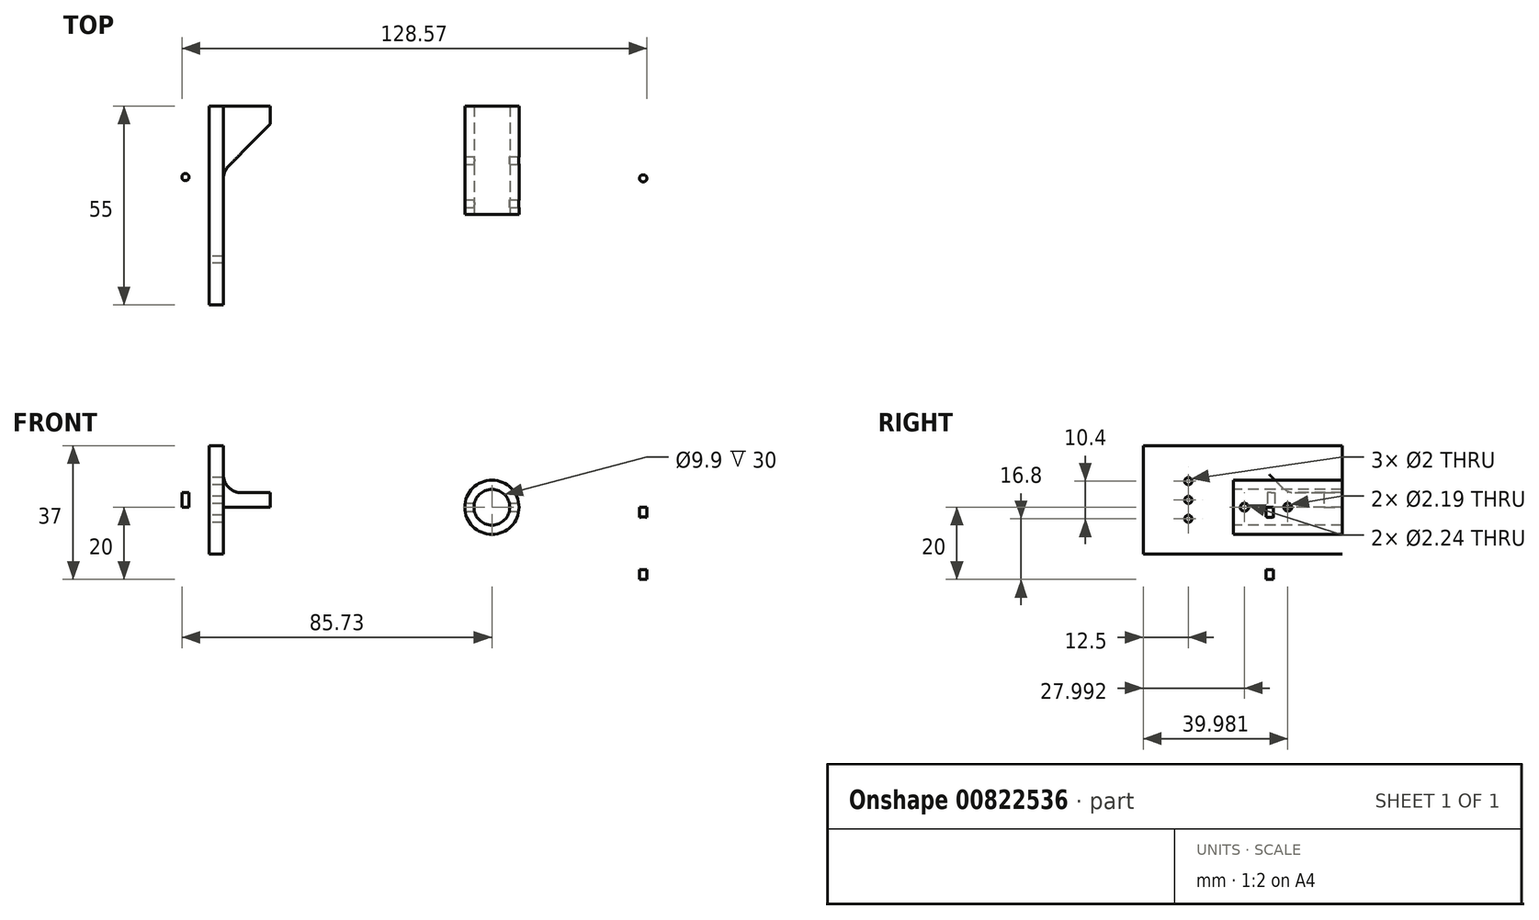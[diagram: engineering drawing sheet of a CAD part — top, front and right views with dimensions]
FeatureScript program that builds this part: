
annotation { "Feature Type Name" : "Feature", "Feature Type Description" : "" }
export const myFeature = defineFeature(function(context is Context, id is Id, definition is map)
    precondition{}
    {
        {
            var Q0;
            Q0=qCreatedBy(makeId("Front.planeOp"),FACE);
            var sketch = newSketch(context, id + "F0", { "sketchPlane" : qUnion([Q0])});
            skCircle(sketch, "E0", {"center": v(0, 0) * mm, "radius": 4.95 * mm});
            skCircle(sketch, "E1", {"center": v(0, 0) * mm, "radius": 7.5 * mm});
            skSolve(sketch);
        }
        {
            var Q0;
            Q0 = qSketchRegion(id + "F0", true);
            extrude(context, id + "F1", {"entities" : qUnion([Q0]), "oppositeDirection" : true, "depth" : 30 * mm, "offsetDistance" : 25 * mm});
        }
        {
            var Q0;
            Q0=qCreatedBy(makeId("Right.planeOp"),FACE);
            cPlane(context, id + "F2", {"entities" : qUnion([Q0]), "cplaneType" : CPlaneType.OFFSET, "offset" : 7.5 * mm, "width" : 150 * mm, "height" : 150 * mm});
        }
        {
            var Q0;
            Q0=qCreatedBy(id+"F2.planeOp",FACE);
            var sketch = newSketch(context, id + "F3", { "sketchPlane" : qUnion([Q0])});
            skLineSegment(sketch, "E2", {"start": v(0, 0) * mm, "end": v(29.96, 0) * mm});
            skLineSegment(sketch, "E3", {"start": v(14.98, 0) * mm, "end": v(14.98, 7.5) * mm});
            skCircle(sketch, "E4", {"center": v(14.98, 0) * mm, "radius": 1.1 * mm});
            skLineSegment(sketch, "E5", {"start": v(0, 0) * mm, "end": v(3, 0) * mm});
            skCircle(sketch, "E6", {"center": v(3, 0) * mm, "radius": 1.12 * mm});
            skSolve(sketch);
        }
        {
            var Q0;
            Q0 = qSketchRegion(id + "F3", true);
            extrude(context, id + "F4", {"entities" : qUnion([Q0]), "operationType" : NewBodyOperationType.REMOVE, "oppositeDirection" : true, "depth" : 25 * mm, "offsetDistance" : 25 * mm});
        }
        {
            var Q0;
            Q0=qCreatedBy(makeId("Front.planeOp"),FACE);
            var sketch = newSketch(context, id + "F5", { "sketchPlane" : qUnion([Q0])});
            skLineSegment(sketch, "E7.bottom", {"start": v(31.94, 0) * mm, "end": v(51.73, 0) * mm});
            skLineSegment(sketch, "E7.top", {"start": v(31.94, -20) * mm, "end": v(51.73, -20) * mm});
            skLineSegment(sketch, "E7.left", {"start": v(31.94, 0) * mm, "end": v(31.94, -20) * mm});
            skLineSegment(sketch, "E7.right", {"start": v(51.73, 0) * mm, "end": v(51.73, -20) * mm});
            skLineSegment(sketch, "E8", {"start": v(41.84, 0) * mm, "end": v(41.84, -20) * mm});
            skLineSegment(sketch, "E9", {"start": v(31.94, -10) * mm, "end": v(51.73, -10) * mm});
            skCircle(sketch, "E10", {"center": v(41.84, -10) * mm, "radius": 7.3 * mm});
            skSolve(sketch);
        }
        {
            var Q0;
            {var subQ1=sQuery(id+"F5.wireOp",EDGE,"E7.left");var subQ6=sQuery(id+"F5.wireOp",EDGE,"E7.bottom");var subQ9=makeQuery(id+"F5.imprint","INTERSECT",VERTEX,{"derivedFrom":[subQ6,subQ1]});Q0=makeQuery(id+"F5.imprint","IMPRINT",FACE,{"disambiguationData":[TD([[makeQuery(id+"F5.imprint","IMPRINT",EDGE,{"disambiguationData":[TD([[subQ9,-1.0]])],"derivedFrom":subQ6}),-1.0]])]});}
            var Q1;
            {var subQ1=sQuery(id+"F5.wireOp",EDGE,"E7.right");var subQ6=sQuery(id+"F5.wireOp",EDGE,"E7.bottom");var subQ9=makeQuery(id+"F5.imprint","INTERSECT",VERTEX,{"derivedFrom":[subQ6,subQ1]});Q1=makeQuery(id+"F5.imprint","IMPRINT",FACE,{"disambiguationData":[TD([[makeQuery(id+"F5.imprint","IMPRINT",EDGE,{"disambiguationData":[TD([[subQ9,1.0]])],"derivedFrom":subQ6}),-1.0]])]});}
            var Q2;
            {var subQ1=sQuery(id+"F5.wireOp",EDGE,"E7.right");var subQ6=sQuery(id+"F5.wireOp",EDGE,"E7.top");var subQ9=makeQuery(id+"F5.imprint","INTERSECT",VERTEX,{"derivedFrom":[subQ6,subQ1]});Q2=makeQuery(id+"F5.imprint","IMPRINT",FACE,{"disambiguationData":[TD([[makeQuery(id+"F5.imprint","IMPRINT",EDGE,{"disambiguationData":[TD([[subQ9,1.0]])],"derivedFrom":subQ6}),1.0]])]});}
            var Q3;
            {var subQ1=sQuery(id+"F5.wireOp",EDGE,"E7.top");var subQ5=sQuery(id+"F5.wireOp",EDGE,"E7.left");var subQ6=makeQuery(id+"F5.imprint","INTERSECT",VERTEX,{"derivedFrom":[subQ1,subQ5]});Q3=makeQuery(id+"F5.imprint","IMPRINT",FACE,{"disambiguationData":[TD([[makeQuery(id+"F5.imprint","IMPRINT",EDGE,{"disambiguationData":[TD([[subQ6,-1.0]])],"derivedFrom":subQ1}),1.0]])]});}
            extrude(context, id + "F6", {"entities" : qUnion([Q0, Q1, Q2, Q3]), "oppositeDirection" : true, "depth" : 20 * mm, "offsetDistance" : 25 * mm});
        }
        {
            var Q0;
            Q0=makeQuery(id+"F6.opExtrude","SWEPT_FACE",FACE,{"disambiguationData":[OSD([sQuery(id+"F5.wireOp",EDGE,"E7.right")])]});
            var sketch = newSketch(context, id + "F7", { "sketchPlane" : qUnion([Q0])});
            skLineSegment(sketch, "E11", {"start": v(10, 0) * mm, "end": v(10, -20) * mm});
            skCircle(sketch, "E12", {"center": v(10, -10) * mm, "radius": 1 * mm});
            skSolve(sketch);
        }
        {
            var Q0;
            Q0 = qSketchRegion(id + "F7", true);
            extrude(context, id + "F8", {"entities" : qUnion([Q0]), "operationType" : NewBodyOperationType.REMOVE, "oppositeDirection" : true, "depth" : 21 * mm, "offsetDistance" : 25 * mm});
        }
        {
            var Q0;
            Q0=makeQuery(id+"F6.opExtrude","SWEPT_FACE",FACE,{"disambiguationData":[OSD([sQuery(id+"F5.wireOp",EDGE,"E7.bottom")])]});
            var sketch = newSketch(context, id + "F9", { "sketchPlane" : qUnion([Q0])});
            skLineSegment(sketch, "E13", {"start": v(41.84, 20) * mm, "end": v(41.84, 0) * mm});
            skCircle(sketch, "E14", {"center": v(41.84, 10) * mm, "radius": 1 * mm});
            skSolve(sketch);
        }
        {
            var Q0;
            {var subQ0=sQuery(id+"F9.wireOp",EDGE,"E14");var subQ1=sQuery(id+"F9.wireOp",EDGE,"E13");var subQ2=makeQuery(id+"F9.imprint","INTERSECT",VERTEX,{"disambiguationData":[OD(0.0)],"derivedFrom":[subQ1,subQ0]});Q0=makeQuery(id+"F9.imprint","IMPRINT",FACE,{"disambiguationData":[TD([[makeQuery(id+"F9.imprint","IMPRINT",EDGE,{"disambiguationData":[TD([[subQ2,-1.0]])],"derivedFrom":subQ1}),1.0]])]});}
            var Q1;
            {var subQ0=sQuery(id+"F9.wireOp",EDGE,"E14");var subQ1=sQuery(id+"F9.wireOp",EDGE,"E13");var subQ2=makeQuery(id+"F9.imprint","INTERSECT",VERTEX,{"disambiguationData":[OD(0.0)],"derivedFrom":[subQ1,subQ0]});Q1=makeQuery(id+"F9.imprint","IMPRINT",FACE,{"disambiguationData":[TD([[makeQuery(id+"F9.imprint","IMPRINT",EDGE,{"disambiguationData":[TD([[subQ2,-1.0]])],"derivedFrom":subQ1}),-1.0]])]});}
            extrude(context, id + "F10", {"entities" : qUnion([Q0, Q1]), "operationType" : NewBodyOperationType.REMOVE, "oppositeDirection" : true, "depth" : 21 * mm, "offsetDistance" : 25 * mm});
        }
        {
            var Q0;
            Q0=qCreatedBy(makeId("Top.planeOp"),FACE);
            var sketch = newSketch(context, id + "F11", { "sketchPlane" : qUnion([Q0])});
            skLineSegment(sketch, "E15.bottom", {"start": v(-61.23, 0) * mm, "end": v(-91.23, 0) * mm});
            skLineSegment(sketch, "E15.top", {"start": v(-61.23, 30) * mm, "end": v(-91.23, 30) * mm});
            skLineSegment(sketch, "E15.left", {"start": v(-61.23, 0) * mm, "end": v(-61.23, 30) * mm});
            skLineSegment(sketch, "E15.right", {"start": v(-91.23, 0) * mm, "end": v(-91.23, 30) * mm});
            skPoint(sketch, "E16", {"position": v(-76.23, 0) * mm});
            skSolve(sketch);
        }
        {
            var Q0;
            Q0=makeQuery(id+"F11.imprint","IMPRINT",FACE,{"disambiguationData":[TD([[makeQuery(id+"F11.imprint","IMPRINT",EDGE,{"derivedFrom":sQuery(id+"F11.wireOp",EDGE,"E15.bottom")}),-1.0]])]});
            extrude(context, id + "F12", {"entities" : qUnion([Q0]), "depth" : 4 * mm, "offsetDistance" : 25 * mm});
        }
        {
            var Q0;
            Q0=makeQuery(id+"F12.opExtrude","SWEPT_FACE",FACE,{"disambiguationData":[OSD([sQuery(id+"F11.wireOp",EDGE,"E15.bottom")])]});
            var sketch = newSketch(context, id + "F13", { "sketchPlane" : qUnion([Q0])});
            skLineSegment(sketch, "E17", {"start": v(-91.23, 4) * mm, "end": v(-61.23, 4) * mm});
            skPoint(sketch, "E18", {"position": v(-76.23, 4) * mm});
            skPoint(sketch, "E19", {"position": v(-78.23, 4) * mm});
            skLineSegment(sketch, "E20.bottom", {"start": v(-78.23, 4) * mm, "end": v(-74.23, 4) * mm});
            skLineSegment(sketch, "E20.top", {"start": v(-78.23, 17) * mm, "end": v(-74.23, 17) * mm});
            skLineSegment(sketch, "E20.left", {"start": v(-78.23, 4) * mm, "end": v(-78.23, 17) * mm});
            skLineSegment(sketch, "E20.right", {"start": v(-74.23, 4) * mm, "end": v(-74.23, 17) * mm});
            skLineSegment(sketch, "E21.bottom", {"start": v(-78.23, 4) * mm, "end": v(-74.47, 4) * mm});
            skLineSegment(sketch, "E22.top", {"start": v(-78.23, -13) * mm, "end": v(-74.23, -13) * mm});
            skLineSegment(sketch, "E22.left", {"start": v(-78.23, 4) * mm, "end": v(-78.23, -13) * mm});
            skLineSegment(sketch, "E22.right", {"start": v(-74.23, 4) * mm, "end": v(-74.23, -13) * mm});
            skSolve(sketch);
        }
        {
            var Q0;
            {var subQ0=sQuery(id+"F13.wireOp",EDGE,"E22.top");Q0=makeQuery(id+"F13.imprint","IMPRINT",FACE,{"disambiguationData":[TD([[makeQuery(id+"F13.imprint","IMPRINT",EDGE,{"derivedFrom":subQ0}),1.0]])]});}
            var Q1;
            {var subQ0=sQuery(id+"F13.wireOp",EDGE,"E22.left");var subQ4=makeQuery(id+"F12.opExtrude","CAP_EDGE",EDGE,{"disambiguationData":[OSD([sQuery(id+"F11.wireOp",EDGE,"E15.bottom")])],"isStart":true});var subQ5=makeQuery(id+"F13.imprint","INTERSECT",VERTEX,{"derivedFrom":[subQ4,subQ0]});Q1=makeQuery(id+"F13.imprint","IMPRINT",FACE,{"disambiguationData":[TD([[makeQuery(id+"F13.imprint","IMPRINT",EDGE,{"disambiguationData":[TD([[subQ5,1.0]])],"derivedFrom":subQ4}),-1.0]])]});}
            var Q2;
            Q2=makeQuery(id+"F13.imprint","IMPRINT",FACE,{"disambiguationData":[TD([[makeQuery(id+"F13.imprint","IMPRINT",EDGE,{"derivedFrom":sQuery(id+"F13.wireOp",EDGE,"E20.top")}),-1.0]])]});
            extrude(context, id + "F14", {"entities" : qUnion([Q0, Q1, Q2]), "operationType" : NewBodyOperationType.ADD, "depth" : 25 * mm, "offsetDistance" : 25 * mm});
        }
        {
            var Q0;
            {var subQ0=sQuery(id+"F13.wireOp",EDGE,"E22.right");var subQ1=sQuery(id+"F13.wireOp",EDGE,"E20.right");var subQ2=sQuery(id+"F13.wireOp",EDGE,"E22.left");var subQ3=sQuery(id+"F13.wireOp",EDGE,"E20.left");var subQ5=sQuery(id+"F13.wireOp",EDGE,"E22.top");Q0=makeQuery(id+"F14.boolean.opBoolean","SPLIT",FACE,{"disambiguationData":[TD([makeQuery(id+"F14.opExtrude","SWEPT_FACE",FACE,{"disambiguationData":[OSD([subQ5])]})])],"derivedFrom":makeQuery(id+"F14.opExtrude","CAP_FACE",FACE,{"disambiguationData":[OSD([sQuery(id+"F13.wireOp",EDGE,"E20.top"),subQ3,subQ1,subQ5,subQ2,subQ0])],"isStart":true})});}
            extrude(context, id + "F15", {"entities" : qUnion([Q0]), "operationType" : NewBodyOperationType.ADD, "depth" : 30 * mm, "offsetDistance" : 25 * mm});
        }
        {
            var Q0;
            {var subQ0=sQuery(id+"F13.wireOp",EDGE,"E22.left");var subQ1=sQuery(id+"F13.wireOp",EDGE,"E20.left");var subQ2=sQuery(id+"F13.wireOp",EDGE,"E20.top");var subQ4=sQuery(id+"F13.wireOp",EDGE,"E22.right");var subQ5=sQuery(id+"F13.wireOp",EDGE,"E20.right");Q0=makeQuery(id+"F14.boolean.opBoolean","SPLIT",FACE,{"disambiguationData":[TD([makeQuery(id+"F14.opExtrude","SWEPT_FACE",FACE,{"disambiguationData":[OSD([subQ2])]})])],"derivedFrom":makeQuery(id+"F14.opExtrude","CAP_FACE",FACE,{"disambiguationData":[OSD([subQ2,subQ1,subQ5,sQuery(id+"F13.wireOp",EDGE,"E22.top"),subQ0,subQ4])],"isStart":true})});}
            extrude(context, id + "F16", {"entities" : qUnion([Q0]), "operationType" : NewBodyOperationType.ADD, "depth" : 30 * mm, "offsetDistance" : 25 * mm});
        }
        {
            var Q0;
            {var subQ0=sQuery(id+"F13.wireOp",EDGE,"E22.left");var subQ1=sQuery(id+"F13.wireOp",EDGE,"E20.left");Q0=makeQuery(id+"F16.boolean.opBoolean","MERGE",FACE,{"derivedFrom":[makeQuery(id+"F15.boolean.opBoolean","MERGE",FACE,{"derivedFrom":[makeQuery(id+"F14.opExtrude","SWEPT_FACE",FACE,{"disambiguationData":[OSD([subQ1,subQ0])]}),makeQuery(id+"F15.opExtrude","SWEPT_FACE",FACE,{"disambiguationData":[OSD([subQ1,subQ0])]})]}),makeQuery(id+"F16.opExtrude","SWEPT_FACE",FACE,{"disambiguationData":[OSD([subQ1,subQ0])]})]});}
            var sketch = newSketch(context, id + "F17", { "sketchPlane" : qUnion([Q0])});
            skLineSegment(sketch, "E23", {"start": v(25, 2) * mm, "end": v(0, 2) * mm});
            skCircle(sketch, "E24", {"center": v(12.5, 2) * mm, "radius": 1 * mm});
            skLineSegment(sketch, "E25", {"start": v(12.5, 2) * mm, "end": v(12.5, -3.2) * mm});
            skCircle(sketch, "E26", {"center": v(12.5, -3.2) * mm, "radius": 1 * mm});
            skLineSegment(sketch, "E27", {"start": v(12.5, 2) * mm, "end": v(12.5, 7.2) * mm});
            skCircle(sketch, "E28", {"center": v(12.5, 7.2) * mm, "radius": 1 * mm});
            skSolve(sketch);
        }
        {
            var Q0;
            Q0 = qSketchRegion(id + "F17", true);
            extrude(context, id + "F18", {"entities" : qUnion([Q0]), "operationType" : NewBodyOperationType.REMOVE, "oppositeDirection" : true, "depth" : 5 * mm, "offsetDistance" : 25 * mm});
        }
        {
            var Q0;
            Q0=makeQuery(id+"F12.opExtrude","SWEPT_EDGE",EDGE,{"disambiguationData":[OSD([sQuery(id+"F11.wireOp",EDGE,"E15.bottom"),sQuery(id+"F11.wireOp",EDGE,"E15.left")])]});
            chamfer(context, id + "F19", {"entities" : qUnion([Q0]), "width" : 25 * mm, "tangentPropagation" : true});
        }
        {
            var Q0;
            {var subQ0=sQuery(id+"F13.wireOp",EDGE,"E22.right");var subQ1=sQuery(id+"F13.wireOp",EDGE,"E20.right");var subQ2=sQuery(id+"F13.wireOp",EDGE,"E22.left");var subQ3=sQuery(id+"F13.wireOp",EDGE,"E22.top");var subQ4=sQuery(id+"F13.wireOp",EDGE,"E20.left");var subQ5=sQuery(id+"F13.wireOp",EDGE,"E20.top");var subQ6=sQuery(id+"F11.wireOp",EDGE,"E15.right");var subQ7=sQuery(id+"F11.wireOp",EDGE,"E15.left");var subQ8=sQuery(id+"F11.wireOp",EDGE,"E15.top");var subQ9=sQuery(id+"F11.wireOp",EDGE,"E15.bottom");Q0=makeQuery(id+"F15.opExtrude","SWEPT_EDGE",EDGE,{"disambiguationData":[OSD([subQ9,subQ8,subQ7,subQ6,subQ5,subQ4,subQ1,subQ3,subQ2,subQ0]),TDD([makeQuery(id+"F14.boolean.opBoolean","TWEAK_VERTEX",VERTEX,{"derivedFrom":[makeQuery(id+"F12.opExtrude","SWEPT_FACE",FACE,{"disambiguationData":[OSD([subQ9])]}),makeQuery(id+"F12.opExtrude","CAP_FACE",FACE,{"disambiguationData":[OSD([subQ9,subQ8,subQ7,subQ6])],"isStart":true}),makeQuery(id+"F14.opExtrude","CAP_FACE",FACE,{"disambiguationData":[OSD([subQ5,subQ4,subQ1,subQ3,subQ2,subQ0])],"isStart":true}),makeQuery(id+"F14.opExtrude","SWEPT_FACE",FACE,{"disambiguationData":[OSD([subQ1,subQ0])]})]})])]});}
            var Q1;
            {var subQ0=sQuery(id+"F13.wireOp",EDGE,"E22.right");var subQ1=sQuery(id+"F13.wireOp",EDGE,"E20.right");Q1=makeQuery(id+"F19.opChamfer","BLEND_EDGE",EDGE,{"blendedFrom":[makeQuery(id+"F12.opExtrude","SWEPT_EDGE",EDGE,{"disambiguationData":[OSD([sQuery(id+"F11.wireOp",EDGE,"E15.bottom"),sQuery(id+"F11.wireOp",EDGE,"E15.left")])]}),makeQuery(id+"F16.boolean.opBoolean","MERGE",FACE,{"derivedFrom":[makeQuery(id+"F15.boolean.opBoolean","MERGE",FACE,{"derivedFrom":[makeQuery(id+"F14.opExtrude","SWEPT_FACE",FACE,{"disambiguationData":[OSD([subQ1,subQ0])]}),makeQuery(id+"F15.opExtrude","SWEPT_FACE",FACE,{"disambiguationData":[OSD([subQ1,subQ0])]})]}),makeQuery(id+"F16.opExtrude","SWEPT_FACE",FACE,{"disambiguationData":[OSD([subQ1,subQ0])]})]})],"blendedInto":[makeQuery(id+"F16.boolean.opBoolean","MERGE",FACE,{"derivedFrom":[makeQuery(id+"F15.boolean.opBoolean","MERGE",FACE,{"derivedFrom":[makeQuery(id+"F14.opExtrude","SWEPT_FACE",FACE,{"disambiguationData":[OSD([subQ1,subQ0])]}),makeQuery(id+"F15.opExtrude","SWEPT_FACE",FACE,{"disambiguationData":[OSD([subQ1,subQ0])]})]}),makeQuery(id+"F16.opExtrude","SWEPT_FACE",FACE,{"disambiguationData":[OSD([subQ1,subQ0])]})]})]});}
            var Q2;
            {var subQ0=sQuery(id+"F13.wireOp",EDGE,"E22.right");var subQ1=sQuery(id+"F13.wireOp",EDGE,"E20.right");var subQ2=sQuery(id+"F13.wireOp",EDGE,"E22.left");var subQ3=sQuery(id+"F13.wireOp",EDGE,"E22.top");var subQ4=sQuery(id+"F13.wireOp",EDGE,"E20.left");var subQ5=sQuery(id+"F13.wireOp",EDGE,"E20.top");var subQ6=sQuery(id+"F11.wireOp",EDGE,"E15.right");var subQ7=sQuery(id+"F11.wireOp",EDGE,"E15.left");var subQ8=sQuery(id+"F11.wireOp",EDGE,"E15.top");var subQ9=sQuery(id+"F11.wireOp",EDGE,"E15.bottom");Q2=makeQuery(id+"F16.opExtrude","SWEPT_EDGE",EDGE,{"disambiguationData":[OSD([subQ9,subQ8,subQ7,subQ6,subQ5,subQ4,subQ1,subQ3,subQ2,subQ0]),TDD([makeQuery(id+"F14.boolean.opBoolean","TWEAK_VERTEX",VERTEX,{"derivedFrom":[makeQuery(id+"F12.opExtrude","SWEPT_FACE",FACE,{"disambiguationData":[OSD([subQ9])]}),makeQuery(id+"F12.opExtrude","CAP_FACE",FACE,{"disambiguationData":[OSD([subQ9,subQ8,subQ7,subQ6])],"isStart":false}),makeQuery(id+"F14.opExtrude","CAP_FACE",FACE,{"disambiguationData":[OSD([subQ5,subQ4,subQ1,subQ3,subQ2,subQ0])],"isStart":true}),makeQuery(id+"F14.opExtrude","SWEPT_FACE",FACE,{"disambiguationData":[OSD([subQ1,subQ0])]})]})])]});}
            fillet(context, id + "F20", {"entities" : qUnion([Q0, Q1, Q2]), "radius" : 5 * mm, "tangentPropagation" : true, "allowEdgeOverflow" : false});
        }
        {
            var Q0;
            {var subQ2=sQuery(id+"F11.wireOp",EDGE,"E15.top");var subQ3=sQuery(id+"F11.wireOp",EDGE,"E15.right");var subQ4=sQuery(id+"F11.wireOp",EDGE,"E15.bottom");Q0=makeQuery(id+"F15.boolean.opBoolean","SPLIT",FACE,{"disambiguationData":[TD([makeQuery(id+"F12.opExtrude","SWEPT_FACE",FACE,{"disambiguationData":[OSD([subQ3])]})])],"derivedFrom":makeQuery(id+"F12.opExtrude","CAP_FACE",FACE,{"disambiguationData":[OSD([subQ4,subQ2,sQuery(id+"F11.wireOp",EDGE,"E15.left"),subQ3])],"isStart":true})});}
            var sketch = newSketch(context, id + "F21", { "sketchPlane" : qUnion([Q0])});
            skLineSegment(sketch, "E29", {"start": v(-84.73, -30) * mm, "end": v(-84.73, 0) * mm});
            skCircle(sketch, "E30", {"center": v(-84.73, -25) * mm, "radius": 1 * mm});
            skCircle(sketch, "E31", {"center": v(-84.73, -19.87) * mm, "radius": 1 * mm});
            skCircle(sketch, "E32", {"center": v(-84.73, -14.87) * mm, "radius": 1 * mm});
            skCircle(sketch, "E33", {"center": v(-84.73, -10.35) * mm, "radius": 1 * mm});
            skSolve(sketch);
        }
        {
            var Q0;
            {var subQ0=sQuery(id+"F21.wireOp",EDGE,"E30");var subQ1=sQuery(id+"F21.wireOp",EDGE,"E29");var subQ2=makeQuery(id+"F21.imprint","INTERSECT",VERTEX,{"disambiguationData":[OD(0.0)],"derivedFrom":[subQ1,subQ0]});Q0=makeQuery(id+"F21.imprint","IMPRINT",FACE,{"disambiguationData":[TD([[makeQuery(id+"F21.imprint","IMPRINT",EDGE,{"disambiguationData":[TD([[subQ2,-1.0]])],"derivedFrom":subQ1}),1.0]])]});}
            var Q1;
            {var subQ0=sQuery(id+"F21.wireOp",EDGE,"E30");var subQ1=sQuery(id+"F21.wireOp",EDGE,"E29");var subQ2=makeQuery(id+"F21.imprint","INTERSECT",VERTEX,{"disambiguationData":[OD(0.0)],"derivedFrom":[subQ1,subQ0]});Q1=makeQuery(id+"F21.imprint","IMPRINT",FACE,{"disambiguationData":[TD([[makeQuery(id+"F21.imprint","IMPRINT",EDGE,{"disambiguationData":[TD([[subQ2,-1.0]])],"derivedFrom":subQ1}),-1.0]])]});}
            var Q2;
            {var subQ0=sQuery(id+"F21.wireOp",EDGE,"E31");var subQ1=sQuery(id+"F21.wireOp",EDGE,"E29");var subQ2=makeQuery(id+"F21.imprint","INTERSECT",VERTEX,{"disambiguationData":[OD(0.0)],"derivedFrom":[subQ1,subQ0]});Q2=makeQuery(id+"F21.imprint","IMPRINT",FACE,{"disambiguationData":[TD([[makeQuery(id+"F21.imprint","IMPRINT",EDGE,{"disambiguationData":[TD([[subQ2,-1.0]])],"derivedFrom":subQ1}),1.0]])]});}
            var Q3;
            {var subQ0=sQuery(id+"F21.wireOp",EDGE,"E31");var subQ1=sQuery(id+"F21.wireOp",EDGE,"E29");var subQ2=makeQuery(id+"F21.imprint","INTERSECT",VERTEX,{"disambiguationData":[OD(0.0)],"derivedFrom":[subQ1,subQ0]});Q3=makeQuery(id+"F21.imprint","IMPRINT",FACE,{"disambiguationData":[TD([[makeQuery(id+"F21.imprint","IMPRINT",EDGE,{"disambiguationData":[TD([[subQ2,-1.0]])],"derivedFrom":subQ1}),-1.0]])]});}
            var Q4;
            {var subQ0=sQuery(id+"F21.wireOp",EDGE,"E32");var subQ1=sQuery(id+"F21.wireOp",EDGE,"E29");var subQ2=makeQuery(id+"F21.imprint","INTERSECT",VERTEX,{"disambiguationData":[OD(0.0)],"derivedFrom":[subQ1,subQ0]});Q4=makeQuery(id+"F21.imprint","IMPRINT",FACE,{"disambiguationData":[TD([[makeQuery(id+"F21.imprint","IMPRINT",EDGE,{"disambiguationData":[TD([[subQ2,-1.0]])],"derivedFrom":subQ1}),1.0]])]});}
            var Q5;
            {var subQ0=sQuery(id+"F21.wireOp",EDGE,"E32");var subQ1=sQuery(id+"F21.wireOp",EDGE,"E29");var subQ2=makeQuery(id+"F21.imprint","INTERSECT",VERTEX,{"disambiguationData":[OD(0.0)],"derivedFrom":[subQ1,subQ0]});Q5=makeQuery(id+"F21.imprint","IMPRINT",FACE,{"disambiguationData":[TD([[makeQuery(id+"F21.imprint","IMPRINT",EDGE,{"disambiguationData":[TD([[subQ2,-1.0]])],"derivedFrom":subQ1}),-1.0]])]});}
            var Q6;
            {var subQ0=sQuery(id+"F21.wireOp",EDGE,"E33");var subQ1=sQuery(id+"F21.wireOp",EDGE,"E29");var subQ2=makeQuery(id+"F21.imprint","INTERSECT",VERTEX,{"disambiguationData":[OD(0.0)],"derivedFrom":[subQ1,subQ0]});Q6=makeQuery(id+"F21.imprint","IMPRINT",FACE,{"disambiguationData":[TD([[makeQuery(id+"F21.imprint","IMPRINT",EDGE,{"disambiguationData":[TD([[subQ2,-1.0]])],"derivedFrom":subQ1}),1.0]])]});}
            var Q7;
            {var subQ0=sQuery(id+"F21.wireOp",EDGE,"E33");var subQ1=sQuery(id+"F21.wireOp",EDGE,"E29");var subQ2=makeQuery(id+"F21.imprint","INTERSECT",VERTEX,{"disambiguationData":[OD(0.0)],"derivedFrom":[subQ1,subQ0]});Q7=makeQuery(id+"F21.imprint","IMPRINT",FACE,{"disambiguationData":[TD([[makeQuery(id+"F21.imprint","IMPRINT",EDGE,{"disambiguationData":[TD([[subQ2,-1.0]])],"derivedFrom":subQ1}),-1.0]])]});}
            extrude(context, id + "F22", {"entities" : qUnion([Q0, Q1, Q2, Q3, Q4, Q5, Q6, Q7]), "operationType" : NewBodyOperationType.REMOVE, "oppositeDirection" : true, "depth" : 5 * mm, "offsetDistance" : 25 * mm});
        }
    });
